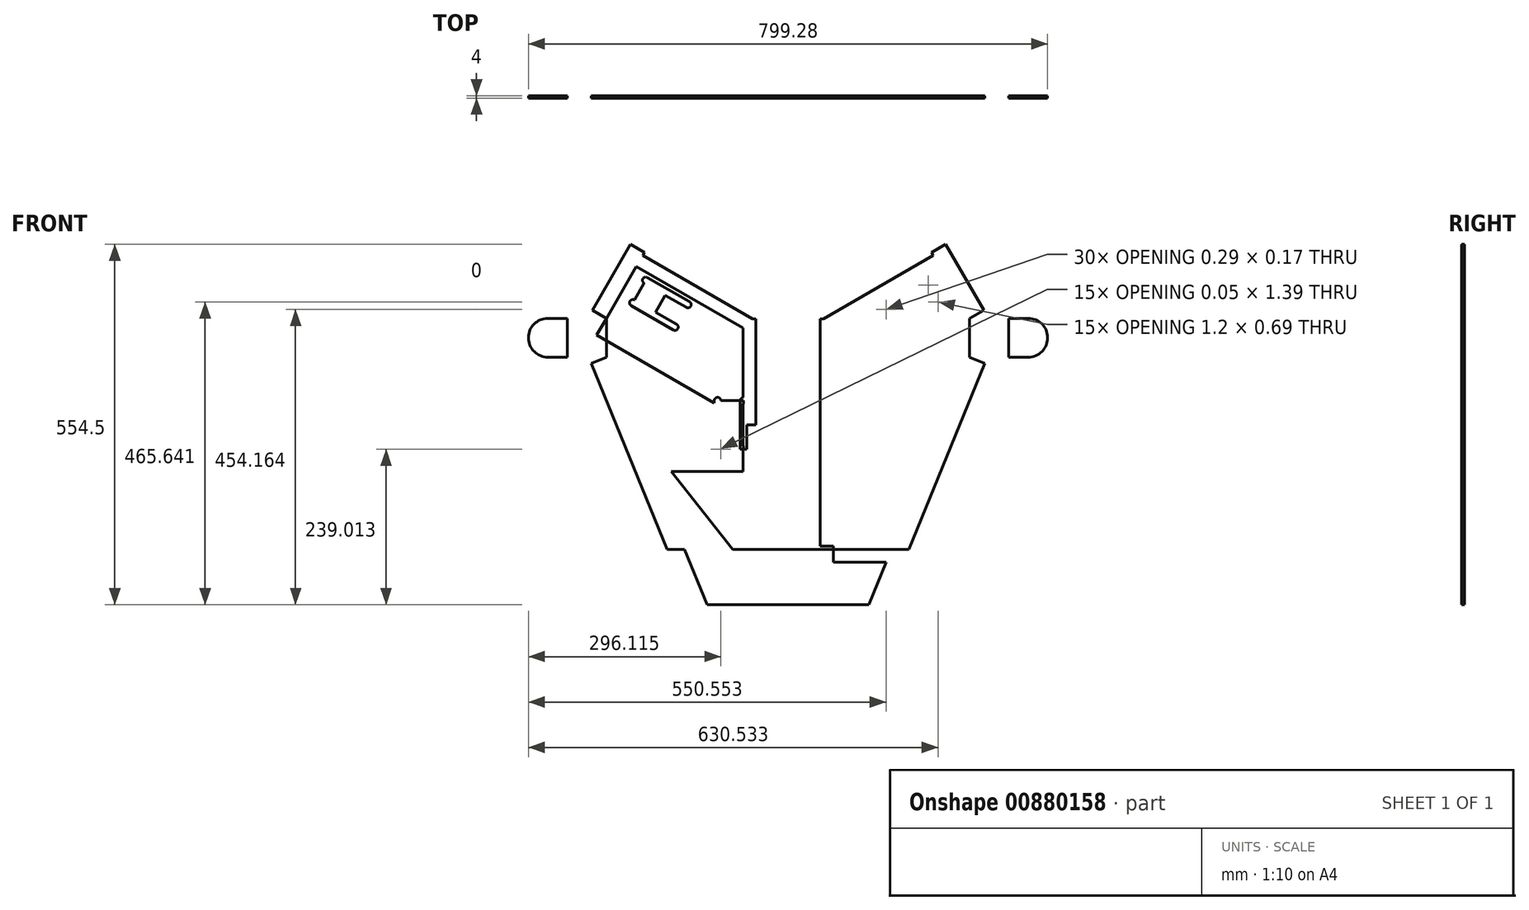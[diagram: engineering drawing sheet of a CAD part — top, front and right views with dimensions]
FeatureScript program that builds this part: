
annotation { "Feature Type Name" : "Feature", "Feature Type Description" : "" }
export const myFeature = defineFeature(function(context is Context, id is Id, definition is map)
    precondition{}
    {
        {
            var Q0;
            Q0=qCreatedBy(makeId("Front.planeOp"),FACE);
            var sketch = newSketch(context, id + "F0", { "sketchPlane" : qUnion([Q0])});
            skLineSegment(sketch, "E0", {"start": v(-53.14, 78.62) * mm, "end": v(-53.14, -271.38) * mm});
            skLineSegment(sketch, "E1", {"start": v(-53.14, -271.38) * mm, "end": v(-28.14, -271.38) * mm});
            skLineSegment(sketch, "E2", {"start": v(-28.14, -271.38) * mm, "end": v(-28.14, 78.62) * mm});
            skLineSegment(sketch, "E3", {"start": v(-28.14, 78.62) * mm, "end": v(-53.14, 78.62) * mm});
            skLineSegment(sketch, "E4", {"start": v(-28.14, 78.62) * mm, "end": v(-331.25, 253.62) * mm});
            skLineSegment(sketch, "E5", {"start": v(-331.25, 253.62) * mm, "end": v(-343.75, 231.97) * mm});
            skLineSegment(sketch, "E6", {"start": v(-343.75, 231.97) * mm, "end": v(-53.14, 64.19) * mm});
            skLineSegment(sketch, "E7", {"start": v(-53.14, -271.38) * mm, "end": v(-53.14, -296.38) * mm});
            skLineSegment(sketch, "E8", {"start": v(-53.14, -296.38) * mm, "end": v(85.86, -296.38) * mm});
            skLineSegment(sketch, "E9", {"start": v(85.86, -296.38) * mm, "end": v(85.86, -271.38) * mm});
            skLineSegment(sketch, "E10", {"start": v(85.86, -271.38) * mm, "end": v(-28.14, -271.38) * mm});
            skLineSegment(sketch, "E11", {"start": v(85.86, -271.38) * mm, "end": v(85.86, 78.62) * mm});
            skLineSegment(sketch, "E12", {"start": v(85.86, 78.62) * mm, "end": v(60.86, 78.62) * mm});
            skLineSegment(sketch, "E13", {"start": v(60.86, 78.62) * mm, "end": v(60.86, -271.38) * mm});
            skLineSegment(sketch, "E14", {"start": v(60.86, 78.62) * mm, "end": v(363.97, 253.62) * mm});
            skLineSegment(sketch, "E15", {"start": v(363.97, 253.62) * mm, "end": v(376.47, 231.97) * mm});
            skLineSegment(sketch, "E16", {"start": v(376.47, 231.97) * mm, "end": v(85.86, 64.19) * mm});
            skLineSegment(sketch, "E17", {"start": v(-331.25, 253.62) * mm, "end": v(-333.75, 249.3) * mm});
            skLineSegment(sketch, "E18", {"start": v(-333.75, 249.3) * mm, "end": v(-38.14, 78.62) * mm});
            skLineSegment(sketch, "E19", {"start": v(-28.14, 78.62) * mm, "end": v(-33.14, 78.62) * mm});
            skLineSegment(sketch, "E20", {"start": v(-33.14, 78.62) * mm, "end": v(-33.14, -271.38) * mm});
            skLineSegment(sketch, "E21", {"start": v(-53.14, -271.38) * mm, "end": v(-53.14, -276.38) * mm});
            skLineSegment(sketch, "E22", {"start": v(-53.14, -276.38) * mm, "end": v(85.86, -276.38) * mm});
            skLineSegment(sketch, "E23", {"start": v(60.86, -271.38) * mm, "end": v(65.86, -271.38) * mm});
            skLineSegment(sketch, "E24", {"start": v(65.86, -271.38) * mm, "end": v(65.86, 78.62) * mm});
            skPoint(sketch, "E24.endSnap0", {"position": v(73.36, 78.62) * mm});
            skLineSegment(sketch, "E25", {"start": v(363.97, 253.62) * mm, "end": v(366.47, 249.3) * mm});
            skLineSegment(sketch, "E26", {"start": v(366.47, 249.3) * mm, "end": v(70.86, 78.62) * mm});
            skLineSegment(sketch, "E27", {"start": v(-176.95, 121.87) * mm, "end": v(-228.9, 151.87) * mm});
            skLineSegment(sketch, "E28", {"start": v(-305.46, 69.05) * mm, "end": v(-53.14, -76.62) * mm});
            skLineSegment(sketch, "E29", {"start": v(-53.14, -51.52) * mm, "end": v(-53.14, -71.28) * mm});
            skLineSegment(sketch, "E30", {"start": v(-53.14, -71.28) * mm, "end": v(-53.14, -131.28) * mm});
            skLineSegment(sketch, "E31", {"start": v(-53.14, -156.38) * mm, "end": v(-163.14, -156.38) * mm});
            skLineSegment(sketch, "E32", {"start": v(-163.14, -156.38) * mm, "end": v(-163.14, -13.11) * mm});
            skLineSegment(sketch, "E33", {"start": v(-163.14, -156.38) * mm, "end": v(-53.14, -296.38) * mm});
            skLineSegment(sketch, "E34", {"start": v(85.86, -156.38) * mm, "end": v(195.86, -156.38) * mm});
            skLineSegment(sketch, "E35", {"start": v(195.86, -156.38) * mm, "end": v(85.86, -296.38) * mm});
            skLineSegment(sketch, "E36", {"start": v(195.86, -156.38) * mm, "end": v(195.86, -13.11) * mm});
            skLineSegment(sketch, "E37", {"start": v(85.86, -76.62) * mm, "end": v(195.86, -13.11) * mm});
            skLineSegment(sketch, "E38", {"start": v(195.86, -13.11) * mm, "end": v(338.18, 69.05) * mm});
            skLineSegment(sketch, "E39", {"start": v(-250.4, 178.08) * mm, "end": v(-237.9, 199.73) * mm});
            skLineSegment(sketch, "E40", {"start": v(277.2, 174.66) * mm, "end": v(264.7, 196.31) * mm});
            skLineSegment(sketch, "E41", {"start": v(264.7, 196.31) * mm, "end": v(338.18, 196.31) * mm});
            skLineSegment(sketch, "E42", {"start": v(-108.14, -226.38) * mm, "end": v(-108.14, -296.38) * mm});
            skLineSegment(sketch, "E43", {"start": v(-108.14, -296.38) * mm, "end": v(-53.14, -296.38) * mm});
            skLineSegment(sketch, "E44", {"start": v(85.86, -296.38) * mm, "end": v(140.86, -296.38) * mm});
            skPoint(sketch, "E44.endSnap0", {"position": v(140.86, -226.38) * mm});
            skLineSegment(sketch, "E45", {"start": v(140.86, -296.38) * mm, "end": v(140.86, -226.38) * mm});
            skLineSegment(sketch, "E46", {"start": v(-158.2, 139.92) * mm, "end": v(-208.2, 53.31) * mm});
            skLineSegment(sketch, "E47", {"start": v(-158.2, 139.92) * mm, "end": v(-168.95, 121.3) * mm});
            skLineSegment(sketch, "E48", {"start": v(-168.95, 121.3) * mm, "end": v(-201.42, 140.05) * mm});
            skLineSegment(sketch, "E49", {"start": v(-201.42, 140.05) * mm, "end": v(-202.67, 137.88) * mm});
            skLineSegment(sketch, "E50", {"start": v(-202.67, 137.88) * mm, "end": v(-137.72, 100.38) * mm});
            skCircle(sketch, "E51", {"center": v(-202.67, 137.88) * mm, "radius": 5 * mm});
            skCircle(sketch, "E52", {"center": v(-137.72, 100.38) * mm, "radius": 5 * mm});
            skLineSegment(sketch, "E53", {"start": v(-135.37, 104.8) * mm, "end": v(-140.07, 95.97) * mm});
            skLineSegment(sketch, "E54", {"start": v(-140.07, 95.97) * mm, "end": v(-205.31, 133.64) * mm});
            skLineSegment(sketch, "E55", {"start": v(-202.67, 137.88) * mm, "end": v(-222.67, 103.24) * mm});
            skLineSegment(sketch, "E56", {"start": v(-222.67, 103.24) * mm, "end": v(-157.72, 65.74) * mm});
            skCircle(sketch, "E57", {"center": v(-222.67, 103.24) * mm, "radius": 5 * mm});
            skCircle(sketch, "E58", {"center": v(-157.72, 65.74) * mm, "radius": 5 * mm});
            skLineSegment(sketch, "E59", {"start": v(-155.22, 70.07) * mm, "end": v(-220.17, 107.57) * mm});
            skLineSegment(sketch, "E60", {"start": v(-220.17, 107.57) * mm, "end": v(-225.17, 98.9) * mm});
            skLineSegment(sketch, "E61", {"start": v(-225.17, 98.9) * mm, "end": v(-160.22, 61.4) * mm});
            skLineSegment(sketch, "E62", {"start": v(-200.1, 142.17) * mm, "end": v(-135.37, 104.8) * mm});
            skLineSegment(sketch, "E63", {"start": v(-28.14, -84.86) * mm, "end": v(-49.64, -84.86) * mm});
            skLineSegment(sketch, "E64", {"start": v(-49.64, -84.86) * mm, "end": v(-49.64, -47.36) * mm});
            skLineSegment(sketch, "E65", {"start": v(-49.64, -47.36) * mm, "end": v(-52.14, -47.36) * mm});
            skLineSegment(sketch, "E66", {"start": v(-52.14, -47.36) * mm, "end": v(-52.14, -122.36) * mm});
            skCircle(sketch, "E67", {"center": v(-52.14, -47.36) * mm, "radius": 5 * mm});
            skCircle(sketch, "E68", {"center": v(-52.14, -122.36) * mm, "radius": 5 * mm});
            skLineSegment(sketch, "E69", {"start": v(-47.14, -122.2) * mm, "end": v(-57.14, -122.53) * mm});
            skLineSegment(sketch, "E70", {"start": v(-57.14, -122.53) * mm, "end": v(-57.14, -47.2) * mm});
            skLineSegment(sketch, "E71", {"start": v(-52.14, -47.36) * mm, "end": v(-92.14, -47.36) * mm});
            skLineSegment(sketch, "E72", {"start": v(-92.14, -47.36) * mm, "end": v(-92.14, -122.36) * mm});
            skCircle(sketch, "E73", {"center": v(-92.14, -47.36) * mm, "radius": 5 * mm});
            skCircle(sketch, "E74", {"center": v(-92.14, -122.36) * mm, "radius": 5 * mm});
            skLineSegment(sketch, "E75", {"start": v(-87.19, -123.06) * mm, "end": v(-87.14, -47.36) * mm});
            skLineSegment(sketch, "E76", {"start": v(-87.14, -47.36) * mm, "end": v(-97.14, -47.36) * mm});
            skLineSegment(sketch, "E77", {"start": v(-97.14, -47.36) * mm, "end": v(-97.14, -122.36) * mm});
            skLineSegment(sketch, "E78", {"start": v(-47.14, -47.44) * mm, "end": v(-47.14, -122.2) * mm});
            skLineSegment(sketch, "E79", {"start": v(185.25, 136.65) * mm, "end": v(196, 118.03) * mm});
            skLineSegment(sketch, "E80", {"start": v(196, 118.03) * mm, "end": v(163.52, 99.28) * mm});
            skLineSegment(sketch, "E81", {"start": v(163.52, 99.28) * mm, "end": v(164.77, 97.11) * mm});
            skLineSegment(sketch, "E82", {"start": v(164.77, 97.11) * mm, "end": v(229.73, 134.61) * mm});
            skCircle(sketch, "E83", {"center": v(164.77, 97.11) * mm, "radius": 5 * mm});
            skCircle(sketch, "E84", {"center": v(229.73, 134.61) * mm, "radius": 5 * mm});
            skLineSegment(sketch, "E85", {"start": v(227.08, 138.86) * mm, "end": v(232.37, 130.37) * mm});
            skLineSegment(sketch, "E86", {"start": v(232.37, 130.37) * mm, "end": v(167.13, 92.7) * mm});
            skLineSegment(sketch, "E87", {"start": v(164.77, 97.11) * mm, "end": v(184.77, 62.47) * mm});
            skLineSegment(sketch, "E88", {"start": v(184.77, 62.47) * mm, "end": v(249.73, 99.97) * mm});
            skCircle(sketch, "E89", {"center": v(184.77, 62.47) * mm, "radius": 5 * mm});
            skCircle(sketch, "E90", {"center": v(249.73, 99.97) * mm, "radius": 5 * mm});
            skLineSegment(sketch, "E91", {"start": v(247.86, 104.6) * mm, "end": v(182.27, 66.8) * mm});
            skLineSegment(sketch, "E92", {"start": v(182.27, 66.8) * mm, "end": v(187.27, 58.14) * mm});
            skLineSegment(sketch, "E93", {"start": v(187.27, 58.14) * mm, "end": v(252.23, 95.64) * mm});
            skLineSegment(sketch, "E94", {"start": v(162.34, 101.48) * mm, "end": v(227.08, 138.86) * mm});
            skLineSegment(sketch, "E95", {"start": v(185.25, 136.65) * mm, "end": v(158.33, 121.1) * mm});
            skLineSegment(sketch, "E96", {"start": v(-158.2, 139.92) * mm, "end": v(-136.54, 127.42) * mm});
            skLineSegment(sketch, "E97", {"start": v(-28.14, -84.86) * mm, "end": v(-28.14, -59.86) * mm});
            skLineSegment(sketch, "E98", {"start": v(-208.2, 53.31) * mm, "end": v(-208.2, -33.23) * mm});
            skLineSegment(sketch, "E99", {"start": v(-208.2, -33.23) * mm, "end": v(-163.14, -33.23) * mm});
            skLineSegment(sketch, "E100", {"start": v(195.86, -33.23) * mm, "end": v(240.91, -33.23) * mm});
            skLineSegment(sketch, "E101", {"start": v(240.91, -33.23) * mm, "end": v(240.91, 12.9) * mm});
            skLineSegment(sketch, "E102", {"start": v(-208.2, 12.9) * mm, "end": v(-208.2, 32.9) * mm});
            skLineSegment(sketch, "E103", {"start": v(240.91, 12.9) * mm, "end": v(240.91, 32.9) * mm});
            skLineSegment(sketch, "E104", {"start": v(-163.14, -84.74) * mm, "end": v(-180.4, -84.74) * mm});
            skLineSegment(sketch, "E105", {"start": v(-180.4, -84.74) * mm, "end": v(-180.4, -33.23) * mm});
            skLineSegment(sketch, "E106", {"start": v(-28.14, 78.62) * mm, "end": v(-204.8, 180.62) * mm});
            skLineSegment(sketch, "E107", {"start": v(-204.8, 180.62) * mm, "end": v(-278.28, 53.37) * mm});
            skLineSegment(sketch, "E108", {"start": v(60.86, 78.62) * mm, "end": v(237.53, 180.62) * mm});
            skLineSegment(sketch, "E109", {"start": v(237.53, 180.62) * mm, "end": v(311, 53.37) * mm});
            skLineSegment(sketch, "E110", {"start": v(-108.14, -296.38) * mm, "end": v(-108.14, -361.38) * mm});
            skLineSegment(sketch, "E111", {"start": v(-108.14, -361.38) * mm, "end": v(140.86, -361.38) * mm});
            skLineSegment(sketch, "E112", {"start": v(140.86, -361.38) * mm, "end": v(140.86, -296.38) * mm});
            skLineSegment(sketch, "E113", {"start": v(-278.28, 53.37) * mm, "end": v(-263.28, 79.35) * mm});
            skLineSegment(sketch, "E114", {"start": v(-263.28, 79.35) * mm, "end": v(-323.28, 79.35) * mm});
            skLineSegment(sketch, "E115", {"start": v(-323.28, 79.35) * mm, "end": v(-323.28, 19.35) * mm});
            skLineSegment(sketch, "E116", {"start": v(-323.28, 19.35) * mm, "end": v(-219.36, 19.35) * mm});
            skLineSegment(sketch, "E117", {"start": v(311, 53.37) * mm, "end": v(296, 79.35) * mm});
            skLineSegment(sketch, "E118", {"start": v(296, 79.35) * mm, "end": v(356, 79.35) * mm});
            skLineSegment(sketch, "E119", {"start": v(356, 79.35) * mm, "end": v(356, 19.35) * mm});
            skLineSegment(sketch, "E120", {"start": v(356, 19.35) * mm, "end": v(252.08, 19.35) * mm});
            skLineSegment(sketch, "E121", {"start": v(-263.28, 79.35) * mm, "end": v(-263.28, 19.35) * mm});
            skLineSegment(sketch, "E122", {"start": v(-263.28, 19.35) * mm, "end": v(-108.14, -361.38) * mm});
            skLineSegment(sketch, "E123", {"start": v(296, 79.35) * mm, "end": v(296, 19.35) * mm});
            skLineSegment(sketch, "E124", {"start": v(296, 19.35) * mm, "end": v(140.86, -361.38) * mm});
            skLineSegment(sketch, "E125", {"start": v(-28.14, -271.38) * mm, "end": v(-28.14, -251.38) * mm});
            skLineSegment(sketch, "E126", {"start": v(-28.14, -251.38) * mm, "end": v(60.86, -251.38) * mm});
            skLineSegment(sketch, "E127", {"start": v(-108.14, -361.38) * mm, "end": v(-108.14, -386.38) * mm});
            skLineSegment(sketch, "E128", {"start": v(-108.14, -386.38) * mm, "end": v(140.86, -386.38) * mm});
            skLineSegment(sketch, "E129", {"start": v(140.86, -386.38) * mm, "end": v(140.86, -361.38) * mm});
            skLineSegment(sketch, "E130", {"start": v(140.86, -361.38) * mm, "end": v(164.01, -370.81) * mm});
            skLineSegment(sketch, "E131", {"start": v(164.01, -370.81) * mm, "end": v(319.15, 9.91) * mm});
            skLineSegment(sketch, "E132", {"start": v(319.15, 9.91) * mm, "end": v(296, 19.35) * mm});
            skLineSegment(sketch, "E133", {"start": v(-108.14, -361.38) * mm, "end": v(-131.3, -370.81) * mm});
            skLineSegment(sketch, "E134", {"start": v(-131.3, -370.81) * mm, "end": v(-286.43, 9.91) * mm});
            skLineSegment(sketch, "E135", {"start": v(-286.43, 9.91) * mm, "end": v(-263.28, 19.35) * mm});
            skLineSegment(sketch, "E136", {"start": v(-323.28, 19.35) * mm, "end": v(-383.28, 19.35) * mm});
            skLineSegment(sketch, "E137", {"start": v(-383.28, 19.35) * mm, "end": v(-383.28, 79.35) * mm});
            skLineSegment(sketch, "E138", {"start": v(-383.28, 79.35) * mm, "end": v(-323.28, 79.35) * mm});
            skCircle(sketch, "E139", {"center": v(-353.28, 49.35) * mm, "radius": 30 * mm});
            skPoint(sketch, "E139.centerSnap0", {"position": v(-383.28, 49.35) * mm});
            skPoint(sketch, "E139.centerSnap1", {"position": v(-353.28, 79.35) * mm});
            skLineSegment(sketch, "E140", {"start": v(-263.28, 79.35) * mm, "end": v(-284.93, 91.85) * mm});
            skLineSegment(sketch, "E141", {"start": v(-284.93, 91.85) * mm, "end": v(-238.96, 171.47) * mm});
            skLineSegment(sketch, "E142", {"start": v(-238.96, 171.47) * mm, "end": v(-226.46, 193.12) * mm});
            skLineSegment(sketch, "E143", {"start": v(-204.8, 180.62) * mm, "end": v(-192.3, 202.27) * mm});
            skLineSegment(sketch, "E144", {"start": v(-28.14, 78.62) * mm, "end": v(-15.64, 100.27) * mm});
            skLineSegment(sketch, "E145", {"start": v(-15.64, 100.27) * mm, "end": v(-192.3, 202.27) * mm});
            skLineSegment(sketch, "E146", {"start": v(60.86, 78.62) * mm, "end": v(48.36, 100.27) * mm});
            skLineSegment(sketch, "E147", {"start": v(237.53, 180.62) * mm, "end": v(225.03, 202.27) * mm});
            skLineSegment(sketch, "E148", {"start": v(225.03, 202.27) * mm, "end": v(48.36, 100.27) * mm});
            skLineSegment(sketch, "E149", {"start": v(296, 79.35) * mm, "end": v(317.65, 91.85) * mm});
            skLineSegment(sketch, "E150", {"start": v(317.65, 91.85) * mm, "end": v(259.18, 193.12) * mm});
            skLineSegment(sketch, "E151", {"start": v(356, 19.35) * mm, "end": v(416, 19.35) * mm});
            skLineSegment(sketch, "E152", {"start": v(416, 19.35) * mm, "end": v(416, 79.35) * mm});
            skLineSegment(sketch, "E153", {"start": v(416, 79.35) * mm, "end": v(356, 79.35) * mm});
            skCircle(sketch, "E154", {"center": v(386, 49.35) * mm, "radius": 30 * mm});
            skPoint(sketch, "E154.centerSnap0", {"position": v(416, 49.35) * mm});
            skPoint(sketch, "E154.centerSnap1", {"position": v(386, 19.35) * mm});
            skLineSegment(sketch, "E155", {"start": v(-108.14, -361.38) * mm, "end": v(-135.14, -361.38) * mm});
            skLineSegment(sketch, "E156", {"start": v(-135.14, -361.38) * mm, "end": v(140.86, -361.38) * mm});
            skLineSegment(sketch, "E157", {"start": v(140.86, -361.38) * mm, "end": v(167.86, -361.38) * mm});
            skLineSegment(sketch, "E158", {"start": v(-108.14, -296.38) * mm, "end": v(-161.62, -296.38) * mm});
            skLineSegment(sketch, "E159", {"start": v(-161.62, -296.38) * mm, "end": v(194.34, -296.38) * mm});
            skLineSegment(sketch, "E160", {"start": v(85.86, -276.38) * mm, "end": v(202.5, -276.38) * mm});
            skLineSegment(sketch, "E161", {"start": v(202.5, -276.38) * mm, "end": v(-169.77, -276.38) * mm});
            skSolve(sketch);
        }
        {
            var Q0;
            Q0=makeQuery(id+"F0.imprint","IMPRINT",FACE,{"disambiguationData":[TD([[makeQuery(id+"F0.imprint","IMPRINT",EDGE,{"derivedFrom":sQuery(id+"F0.wireOp",EDGE,"E106")}),-1.0]])]});
            var Q1;
            Q1=makeQuery(id+"F0.imprint","IMPRINT",FACE,{"disambiguationData":[TD([[makeQuery(id+"F0.imprint","IMPRINT",EDGE,{"derivedFrom":sQuery(id+"F0.wireOp",EDGE,"E108")}),1.0]])]});
            var Q2;
            {var subQ5=sQuery(id+"F0.wireOp",EDGE,"E149");Q2=makeQuery(id+"F0.imprint","IMPRINT",FACE,{"disambiguationData":[TD([[makeQuery(id+"F0.imprint","IMPRINT",EDGE,{"derivedFrom":subQ5}),1.0]])]});}
            var Q3;
            {var subQ0=sQuery(id+"F0.wireOp",EDGE,"E113");Q3=makeQuery(id+"F0.imprint","IMPRINT",FACE,{"disambiguationData":[TD([[makeQuery(id+"F0.imprint","IMPRINT",EDGE,{"derivedFrom":subQ0}),-1.0]])]});}
            var Q4;
            {var subQ0=sQuery(id+"F0.wireOp",EDGE,"E117");Q4=makeQuery(id+"F0.imprint","IMPRINT",FACE,{"disambiguationData":[TD([[makeQuery(id+"F0.imprint","IMPRINT",EDGE,{"derivedFrom":subQ0}),1.0]])]});}
            var Q5;
            {var subQ0=sQuery(id+"F0.wireOp",EDGE,"E138");var subQ3=sQuery(id+"F0.wireOp",EDGE,"E139");var subQ5=makeQuery(id+"F0.imprint","INTERSECT",VERTEX,{"derivedFrom":[subQ0,subQ3]});Q5=makeQuery(id+"F0.imprint","IMPRINT",FACE,{"disambiguationData":[TD([[makeQuery(id+"F0.imprint","IMPRINT",EDGE,{"disambiguationData":[TD([[subQ5,1.0]])],"derivedFrom":subQ3}),-1.0]])]});}
            var Q6;
            {var subQ0=sQuery(id+"F0.wireOp",EDGE,"E136");var subQ3=sQuery(id+"F0.wireOp",EDGE,"E139");var subQ5=makeQuery(id+"F0.imprint","INTERSECT",VERTEX,{"derivedFrom":[subQ0,subQ3]});Q6=makeQuery(id+"F0.imprint","IMPRINT",FACE,{"disambiguationData":[TD([[makeQuery(id+"F0.imprint","IMPRINT",EDGE,{"disambiguationData":[TD([[subQ5,-1.0]])],"derivedFrom":subQ3}),-1.0]])]});}
            var Q7;
            {var subQ0=sQuery(id+"F0.wireOp",EDGE,"E153");var subQ3=sQuery(id+"F0.wireOp",EDGE,"E154");var subQ5=makeQuery(id+"F0.imprint","INTERSECT",VERTEX,{"derivedFrom":[subQ0,subQ3]});Q7=makeQuery(id+"F0.imprint","IMPRINT",FACE,{"disambiguationData":[TD([[makeQuery(id+"F0.imprint","IMPRINT",EDGE,{"disambiguationData":[TD([[subQ5,-1.0]])],"derivedFrom":subQ3}),-1.0]])]});}
            var Q8;
            {var subQ0=sQuery(id+"F0.wireOp",EDGE,"E151");var subQ3=sQuery(id+"F0.wireOp",EDGE,"E154");var subQ5=makeQuery(id+"F0.imprint","INTERSECT",VERTEX,{"derivedFrom":[subQ0,subQ3]});Q8=makeQuery(id+"F0.imprint","IMPRINT",FACE,{"disambiguationData":[TD([[makeQuery(id+"F0.imprint","IMPRINT",EDGE,{"disambiguationData":[TD([[subQ5,1.0]])],"derivedFrom":subQ3}),-1.0]])]});}
            var Q9;
            {var subQ1=sQuery(id+"F0.wireOp",EDGE,"E19");Q9=makeQuery(id+"F0.imprint","IMPRINT",FACE,{"disambiguationData":[TD([[makeQuery(id+"F0.imprint","IMPRINT",EDGE,{"derivedFrom":subQ1}),1.0]])]});}
            var Q10;
            {var subQ3=sQuery(id+"F0.wireOp",EDGE,"E142");var subQ5=sQuery(id+"F0.wireOp",EDGE,"E18");var subQ7=makeQuery(id+"F0.imprint","INTERSECT",VERTEX,{"derivedFrom":[subQ5,subQ3]});Q10=makeQuery(id+"F0.imprint","IMPRINT",FACE,{"disambiguationData":[TD([[makeQuery(id+"F0.imprint","IMPRINT",EDGE,{"disambiguationData":[TD([[subQ7,-1.0]])],"derivedFrom":subQ5}),1.0]])]});}
            var Q11;
            {var subQ0=sQuery(id+"F0.wireOp",EDGE,"E140");Q11=makeQuery(id+"F0.imprint","IMPRINT",FACE,{"disambiguationData":[TD([[makeQuery(id+"F0.imprint","IMPRINT",EDGE,{"derivedFrom":subQ0}),-1.0]])]});}
            var Q12;
            {var subQ0=sQuery(id+"F0.wireOp",EDGE,"E125");Q12=makeQuery(id+"F0.imprint","IMPRINT",FACE,{"disambiguationData":[TD([[makeQuery(id+"F0.imprint","IMPRINT",EDGE,{"derivedFrom":subQ0}),-1.0]])]});}
            var Q13;
            {var subQ3=sQuery(id+"F0.wireOp",EDGE,"E150");var subQ5=sQuery(id+"F0.wireOp",EDGE,"E26");var subQ6=makeQuery(id+"F0.imprint","INTERSECT",VERTEX,{"derivedFrom":[subQ5,subQ3]});Q13=makeQuery(id+"F0.imprint","IMPRINT",FACE,{"disambiguationData":[TD([[makeQuery(id+"F0.imprint","IMPRINT",EDGE,{"disambiguationData":[TD([[subQ6,-1.0]])],"derivedFrom":subQ5}),-1.0]])]});}
            var Q14;
            {var subQ0=sQuery(id+"F0.wireOp",EDGE,"E116");var subQ1=sQuery(id+"F0.wireOp",EDGE,"E28");var subQ2=makeQuery(id+"F0.imprint","INTERSECT",VERTEX,{"derivedFrom":[subQ1,subQ0]});Q14=makeQuery(id+"F0.imprint","IMPRINT",FACE,{"disambiguationData":[TD([[makeQuery(id+"F0.imprint","IMPRINT",EDGE,{"disambiguationData":[TD([[subQ2,1.0]])],"derivedFrom":subQ1}),-1.0]])]});}
            var Q15;
            {var subQ0=sQuery(id+"F0.wireOp",EDGE,"E120");var subQ1=sQuery(id+"F0.wireOp",EDGE,"E38");var subQ2=makeQuery(id+"F0.imprint","INTERSECT",VERTEX,{"derivedFrom":[subQ1,subQ0]});Q15=makeQuery(id+"F0.imprint","IMPRINT",FACE,{"disambiguationData":[TD([[makeQuery(id+"F0.imprint","IMPRINT",EDGE,{"disambiguationData":[TD([[subQ2,-1.0]])],"derivedFrom":subQ1}),-1.0]])]});}
            var Q16;
            {var subQ5=sQuery(id+"F0.wireOp",EDGE,"E125");Q16=makeQuery(id+"F0.imprint","IMPRINT",FACE,{"disambiguationData":[TD([[makeQuery(id+"F0.imprint","IMPRINT",EDGE,{"derivedFrom":subQ5}),1.0]])]});}
            var Q17;
            {var subQ0=sQuery(id+"F0.wireOp",EDGE,"E142");var subQ5=sQuery(id+"F0.wireOp",EDGE,"E18");var subQ6=makeQuery(id+"F0.imprint","INTERSECT",VERTEX,{"derivedFrom":[subQ5,subQ0]});Q17=makeQuery(id+"F0.imprint","IMPRINT",FACE,{"disambiguationData":[TD([[makeQuery(id+"F0.imprint","IMPRINT",EDGE,{"disambiguationData":[TD([[subQ6,-1.0]])],"derivedFrom":subQ5}),-1.0]])]});}
            var Q18;
            {var subQ0=sQuery(id+"F0.wireOp",EDGE,"E23");Q18=makeQuery(id+"F0.imprint","IMPRINT",FACE,{"disambiguationData":[TD([[makeQuery(id+"F0.imprint","IMPRINT",EDGE,{"derivedFrom":subQ0}),1.0]])]});}
            var Q19;
            {var subQ0=sQuery(id+"F0.wireOp",EDGE,"E150");var subQ1=sQuery(id+"F0.wireOp",EDGE,"E16");var subQ2=makeQuery(id+"F0.imprint","INTERSECT",VERTEX,{"derivedFrom":[subQ1,subQ0]});Q19=makeQuery(id+"F0.imprint","IMPRINT",FACE,{"disambiguationData":[TD([[makeQuery(id+"F0.imprint","IMPRINT",EDGE,{"disambiguationData":[TD([[subQ2,-1.0]])],"derivedFrom":subQ1}),-1.0]])]});}
            var Q20;
            {var subQ8=sQuery(id+"F0.wireOp",EDGE,"E113");Q20=makeQuery(id+"F0.imprint","IMPRINT",FACE,{"disambiguationData":[TD([[makeQuery(id+"F0.imprint","IMPRINT",EDGE,{"derivedFrom":subQ8}),1.0]])]});}
            var Q21;
            {var subQ8=sQuery(id+"F0.wireOp",EDGE,"E117");Q21=makeQuery(id+"F0.imprint","IMPRINT",FACE,{"disambiguationData":[TD([[makeQuery(id+"F0.imprint","IMPRINT",EDGE,{"derivedFrom":subQ8}),-1.0]])]});}
            var Q22;
            {var subQ0=sQuery(id+"F0.wireOp",EDGE,"E139");var subQ1=makeQuery(id+"F0.imprint","INTERSECT",VERTEX,{"derivedFrom":[sQuery(id+"F0.wireOp",EDGE,"E138"),subQ0]});Q22=makeQuery(id+"F0.imprint","IMPRINT",FACE,{"disambiguationData":[TD([[makeQuery(id+"F0.imprint","IMPRINT",EDGE,{"disambiguationData":[TD([[subQ1,1.0]])],"derivedFrom":subQ0}),1.0]])]});}
            var Q23;
            {var subQ0=sQuery(id+"F0.wireOp",EDGE,"E154");var subQ1=makeQuery(id+"F0.imprint","INTERSECT",VERTEX,{"derivedFrom":[sQuery(id+"F0.wireOp",EDGE,"E152"),subQ0]});Q23=makeQuery(id+"F0.imprint","IMPRINT",FACE,{"disambiguationData":[TD([[makeQuery(id+"F0.imprint","IMPRINT",EDGE,{"disambiguationData":[TD([[subQ1,-1.0]])],"derivedFrom":subQ0}),1.0]])]});}
            var Q24;
            {var subQ6=sQuery(id+"F0.wireOp",EDGE,"E19");Q24=makeQuery(id+"F0.imprint","IMPRINT",FACE,{"disambiguationData":[TD([[makeQuery(id+"F0.imprint","IMPRINT",EDGE,{"derivedFrom":subQ6}),-1.0]])]});}
            var Q25;
            {var subQ0=sQuery(id+"F0.wireOp",EDGE,"E108");Q25=makeQuery(id+"F0.imprint","IMPRINT",FACE,{"disambiguationData":[TD([[makeQuery(id+"F0.imprint","IMPRINT",EDGE,{"derivedFrom":subQ0}),-1.0]])]});}
            var Q26;
            {var subQ3=sQuery(id+"F0.wireOp",EDGE,"E161");var subQ5=sQuery(id+"F0.wireOp",EDGE,"E124");var subQ6=makeQuery(id+"F0.imprint","INTERSECT",VERTEX,{"derivedFrom":[subQ5,subQ3]});Q26=makeQuery(id+"F0.imprint","IMPRINT",FACE,{"disambiguationData":[TD([[makeQuery(id+"F0.imprint","IMPRINT",EDGE,{"disambiguationData":[TD([[subQ6,-1.0]])],"derivedFrom":subQ5}),-1.0]])]});}
            var Q27;
            {var subQ3=sQuery(id+"F0.wireOp",EDGE,"E161");var subQ5=sQuery(id+"F0.wireOp",EDGE,"E122");var subQ6=makeQuery(id+"F0.imprint","INTERSECT",VERTEX,{"derivedFrom":[subQ5,subQ3]});Q27=makeQuery(id+"F0.imprint","IMPRINT",FACE,{"disambiguationData":[TD([[makeQuery(id+"F0.imprint","IMPRINT",EDGE,{"disambiguationData":[TD([[subQ6,-1.0]])],"derivedFrom":subQ5}),1.0]])]});}
            var Q28;
            {var subQ19=sQuery(id+"F0.wireOp",EDGE,"E102");Q28=makeQuery(id+"F0.imprint","IMPRINT",FACE,{"disambiguationData":[TD([[makeQuery(id+"F0.imprint","IMPRINT",EDGE,{"derivedFrom":subQ19}),1.0]])]});}
            var Q29;
            {var subQ19=sQuery(id+"F0.wireOp",EDGE,"E37");Q29=makeQuery(id+"F0.imprint","IMPRINT",FACE,{"disambiguationData":[TD([[makeQuery(id+"F0.imprint","IMPRINT",EDGE,{"derivedFrom":subQ19}),1.0]])]});}
            var Q30;
            {var subQ24=sQuery(id+"F0.wireOp",EDGE,"E102");Q30=makeQuery(id+"F0.imprint","IMPRINT",FACE,{"disambiguationData":[TD([[makeQuery(id+"F0.imprint","IMPRINT",EDGE,{"derivedFrom":subQ24}),-1.0]])]});}
            var Q31;
            {var subQ4=sQuery(id+"F0.wireOp",EDGE,"E3");var subQ5=sQuery(id+"F0.wireOp",EDGE,"E0");var subQ6=makeQuery(id+"F0.imprint","INTERSECT",VERTEX,{"derivedFrom":[subQ5,subQ4]});Q31=makeQuery(id+"F0.imprint","IMPRINT",FACE,{"disambiguationData":[TD([[makeQuery(id+"F0.imprint","IMPRINT",EDGE,{"disambiguationData":[TD([[subQ6,-1.0]])],"derivedFrom":subQ5}),-1.0]])]});}
            var Q32;
            {var subQ12=sQuery(id+"F0.wireOp",EDGE,"E31");Q32=makeQuery(id+"F0.imprint","IMPRINT",FACE,{"disambiguationData":[TD([[makeQuery(id+"F0.imprint","IMPRINT",EDGE,{"derivedFrom":subQ12}),-1.0]])]});}
            var Q33;
            {var subQ3=sQuery(id+"F0.wireOp",EDGE,"E104");Q33=makeQuery(id+"F0.imprint","IMPRINT",FACE,{"disambiguationData":[TD([[makeQuery(id+"F0.imprint","IMPRINT",EDGE,{"derivedFrom":subQ3}),-1.0]])]});}
            var Q34;
            {var subQ4=sQuery(id+"F0.wireOp",EDGE,"E32");var subQ5=sQuery(id+"F0.wireOp",EDGE,"E28");var subQ6=makeQuery(id+"F0.imprint","INTERSECT",VERTEX,{"derivedFrom":[subQ5,subQ4]});Q34=makeQuery(id+"F0.imprint","IMPRINT",FACE,{"disambiguationData":[TD([[makeQuery(id+"F0.imprint","IMPRINT",EDGE,{"disambiguationData":[TD([[subQ6,1.0]])],"derivedFrom":subQ4}),1.0]])]});}
            var Q35;
            {var subQ0=sQuery(id+"F0.wireOp",EDGE,"E7");Q35=makeQuery(id+"F0.imprint","IMPRINT",FACE,{"disambiguationData":[TD([[makeQuery(id+"F0.imprint","IMPRINT",EDGE,{"derivedFrom":subQ0}),-1.0]])]});}
            var Q36;
            {var subQ5=sQuery(id+"F0.wireOp",EDGE,"E0");var subQ8=sQuery(id+"F0.wireOp",EDGE,"E30");var subQ9=makeQuery(id+"F0.imprint","INTERSECT",VERTEX,{"derivedFrom":[subQ5,subQ8]});Q36=makeQuery(id+"F0.imprint","IMPRINT",FACE,{"disambiguationData":[TD([[makeQuery(id+"F0.imprint","IMPRINT",EDGE,{"disambiguationData":[TD([[subQ9,-1.0]])],"derivedFrom":subQ5}),1.0]])]});}
            var Q37;
            {var subQ3=sQuery(id+"F0.wireOp",EDGE,"E34");Q37=makeQuery(id+"F0.imprint","IMPRINT",FACE,{"disambiguationData":[TD([[makeQuery(id+"F0.imprint","IMPRINT",EDGE,{"derivedFrom":subQ3}),1.0]])]});}
            var Q38;
            {var subQ1=sQuery(id+"F0.wireOp",EDGE,"E34");Q38=makeQuery(id+"F0.imprint","IMPRINT",FACE,{"disambiguationData":[TD([[makeQuery(id+"F0.imprint","IMPRINT",EDGE,{"derivedFrom":subQ1}),-1.0]])]});}
            var Q39;
            {var subQ6=sQuery(id+"F0.wireOp",EDGE,"E24");Q39=makeQuery(id+"F0.imprint","IMPRINT",FACE,{"disambiguationData":[TD([[makeQuery(id+"F0.imprint","IMPRINT",EDGE,{"derivedFrom":subQ6}),-1.0]])]});}
            var Q40;
            {var subQ3=sQuery(id+"F0.wireOp",EDGE,"E100");Q40=makeQuery(id+"F0.imprint","IMPRINT",FACE,{"disambiguationData":[TD([[makeQuery(id+"F0.imprint","IMPRINT",EDGE,{"derivedFrom":subQ3}),1.0]])]});}
            var Q41;
            {var subQ0=sQuery(id+"F0.wireOp",EDGE,"E16");var subQ1=makeQuery(id+"F0.imprint","IMPRINT",VERTEX,{"derivedFrom":subQ0});Q41=makeQuery(id+"F0.imprint","IMPRINT",FACE,{"disambiguationData":[TD([[makeQuery(id+"F0.imprint","IMPRINT",EDGE,{"disambiguationData":[TD([[subQ1,1.0]])],"derivedFrom":subQ0}),-1.0]])]});}
            var Q42;
            {var subQ0=sQuery(id+"F0.wireOp",EDGE,"E42");var subQ1=sQuery(id+"F0.wireOp",EDGE,"E33");var subQ2=makeQuery(id+"F0.imprint","INTERSECT",VERTEX,{"derivedFrom":[subQ1,subQ0]});Q42=makeQuery(id+"F0.imprint","IMPRINT",FACE,{"disambiguationData":[TD([[makeQuery(id+"F0.imprint","IMPRINT",EDGE,{"disambiguationData":[TD([[subQ2,-1.0]])],"derivedFrom":subQ1}),-1.0]])]});}
            var Q43;
            {var subQ0=sQuery(id+"F0.wireOp",EDGE,"E7");Q43=makeQuery(id+"F0.imprint","IMPRINT",FACE,{"disambiguationData":[TD([[makeQuery(id+"F0.imprint","IMPRINT",EDGE,{"derivedFrom":subQ0}),1.0]])]});}
            var Q44;
            {var subQ9=sQuery(id+"F0.wireOp",EDGE,"E21");Q44=makeQuery(id+"F0.imprint","IMPRINT",FACE,{"disambiguationData":[TD([[makeQuery(id+"F0.imprint","IMPRINT",EDGE,{"derivedFrom":subQ9}),1.0]])]});}
            var Q45;
            {var subQ0=sQuery(id+"F0.wireOp",EDGE,"E54");var subQ1=sQuery(id+"F0.wireOp",EDGE,"E46");var subQ2=makeQuery(id+"F0.imprint","INTERSECT",VERTEX,{"derivedFrom":[subQ1,subQ0]});Q45=makeQuery(id+"F0.imprint","IMPRINT",FACE,{"disambiguationData":[TD([[makeQuery(id+"F0.imprint","IMPRINT",EDGE,{"disambiguationData":[TD([[subQ2,-1.0]])],"derivedFrom":subQ1}),-1.0]])]});}
            var Q46;
            {var subQ0=sQuery(id+"F0.wireOp",EDGE,"E59");var subQ1=sQuery(id+"F0.wireOp",EDGE,"E46");var subQ2=makeQuery(id+"F0.imprint","INTERSECT",VERTEX,{"derivedFrom":[subQ1,subQ0]});Q46=makeQuery(id+"F0.imprint","IMPRINT",FACE,{"disambiguationData":[TD([[makeQuery(id+"F0.imprint","IMPRINT",EDGE,{"disambiguationData":[TD([[subQ2,-1.0]])],"derivedFrom":subQ1}),1.0]])]});}
            var Q47;
            {var subQ0=sQuery(id+"F0.wireOp",EDGE,"E56");var subQ1=sQuery(id+"F0.wireOp",EDGE,"E46");var subQ2=makeQuery(id+"F0.imprint","INTERSECT",VERTEX,{"derivedFrom":[subQ1,subQ0]});Q47=makeQuery(id+"F0.imprint","IMPRINT",FACE,{"disambiguationData":[TD([[makeQuery(id+"F0.imprint","IMPRINT",EDGE,{"disambiguationData":[TD([[subQ2,-1.0]])],"derivedFrom":subQ1}),1.0]])]});}
            var Q48;
            {var subQ0=sQuery(id+"F0.wireOp",EDGE,"E58");var subQ1=makeQuery(id+"F0.imprint","INTERSECT",VERTEX,{"derivedFrom":[subQ0,sQuery(id+"F0.wireOp",EDGE,"E59")]});Q48=makeQuery(id+"F0.imprint","IMPRINT",FACE,{"disambiguationData":[TD([[makeQuery(id+"F0.imprint","IMPRINT",EDGE,{"disambiguationData":[TD([[subQ1,-1.0]])],"derivedFrom":subQ0}),1.0]])]});}
            var Q49;
            {var subQ0=sQuery(id+"F0.wireOp",EDGE,"E56");var subQ1=sQuery(id+"F0.wireOp",EDGE,"E46");var subQ2=makeQuery(id+"F0.imprint","INTERSECT",VERTEX,{"derivedFrom":[subQ1,subQ0]});Q49=makeQuery(id+"F0.imprint","IMPRINT",FACE,{"disambiguationData":[TD([[makeQuery(id+"F0.imprint","IMPRINT",EDGE,{"disambiguationData":[TD([[subQ2,-1.0]])],"derivedFrom":subQ1}),-1.0]])]});}
            var Q50;
            {var subQ0=sQuery(id+"F0.wireOp",EDGE,"E59");var subQ1=sQuery(id+"F0.wireOp",EDGE,"E46");var subQ2=makeQuery(id+"F0.imprint","INTERSECT",VERTEX,{"derivedFrom":[subQ1,subQ0]});Q50=makeQuery(id+"F0.imprint","IMPRINT",FACE,{"disambiguationData":[TD([[makeQuery(id+"F0.imprint","IMPRINT",EDGE,{"disambiguationData":[TD([[subQ2,-1.0]])],"derivedFrom":subQ1}),-1.0]])]});}
            var Q51;
            {var subQ5=sQuery(id+"F0.wireOp",EDGE,"E47");var subQ6=sQuery(id+"F0.wireOp",EDGE,"E6");var subQ7=makeQuery(id+"F0.imprint","INTERSECT",VERTEX,{"derivedFrom":[subQ6,subQ5]});Q51=makeQuery(id+"F0.imprint","IMPRINT",FACE,{"disambiguationData":[TD([[makeQuery(id+"F0.imprint","IMPRINT",EDGE,{"disambiguationData":[TD([[subQ7,1.0]])],"derivedFrom":subQ6}),-1.0]])]});}
            var Q52;
            {var subQ4=sQuery(id+"F0.wireOp",EDGE,"E49");Q52=makeQuery(id+"F0.imprint","IMPRINT",FACE,{"disambiguationData":[TD([[makeQuery(id+"F0.imprint","IMPRINT",EDGE,{"derivedFrom":subQ4}),-1.0]])]});}
            var Q53;
            {var subQ0=sQuery(id+"F0.wireOp",EDGE,"E83");var subQ1=sQuery(id+"F0.wireOp",EDGE,"E82");var subQ2=makeQuery(id+"F0.imprint","INTERSECT",VERTEX,{"derivedFrom":[subQ1,subQ0]});Q53=makeQuery(id+"F0.imprint","IMPRINT",FACE,{"disambiguationData":[TD([[makeQuery(id+"F0.imprint","IMPRINT",EDGE,{"disambiguationData":[TD([[subQ2,-1.0]])],"derivedFrom":subQ1}),-1.0]])]});}
            var Q54;
            {var subQ1=sQuery(id+"F0.wireOp",EDGE,"E80");var subQ5=sQuery(id+"F0.wireOp",EDGE,"E79");var subQ6=makeQuery(id+"F0.imprint","INTERSECT",VERTEX,{"derivedFrom":[subQ5,subQ1]});Q54=makeQuery(id+"F0.imprint","IMPRINT",FACE,{"disambiguationData":[TD([[makeQuery(id+"F0.imprint","IMPRINT",EDGE,{"disambiguationData":[TD([[subQ6,1.0]])],"derivedFrom":subQ5}),1.0]])]});}
            var Q55;
            {var subQ0=sQuery(id+"F0.wireOp",EDGE,"E85");var subQ4=makeQuery(id+"F0.imprint","INTERSECT",VERTEX,{"derivedFrom":[sQuery(id+"F0.wireOp",EDGE,"E82"),subQ0]});Q55=makeQuery(id+"F0.imprint","IMPRINT",FACE,{"disambiguationData":[TD([[makeQuery(id+"F0.imprint","IMPRINT",EDGE,{"disambiguationData":[TD([[subQ4,1.0]])],"derivedFrom":subQ0}),1.0]])]});}
            var Q56;
            {var subQ0=sQuery(id+"F0.wireOp",EDGE,"E85");var subQ1=sQuery(id+"F0.wireOp",EDGE,"E82");var subQ2=makeQuery(id+"F0.imprint","INTERSECT",VERTEX,{"derivedFrom":[subQ1,subQ0]});Q56=makeQuery(id+"F0.imprint","IMPRINT",FACE,{"disambiguationData":[TD([[makeQuery(id+"F0.imprint","IMPRINT",EDGE,{"disambiguationData":[TD([[subQ2,1.0]])],"derivedFrom":subQ1}),1.0]])]});}
            var Q57;
            {var subQ0=sQuery(id+"F0.wireOp",EDGE,"E85");var subQ1=sQuery(id+"F0.wireOp",EDGE,"E82");var subQ2=makeQuery(id+"F0.imprint","INTERSECT",VERTEX,{"derivedFrom":[subQ1,subQ0]});Q57=makeQuery(id+"F0.imprint","IMPRINT",FACE,{"disambiguationData":[TD([[makeQuery(id+"F0.imprint","IMPRINT",EDGE,{"disambiguationData":[TD([[subQ2,1.0]])],"derivedFrom":subQ1}),-1.0]])]});}
            var Q58;
            {var subQ0=sQuery(id+"F0.wireOp",EDGE,"E80");var subQ1=sQuery(id+"F0.wireOp",EDGE,"E79");var subQ2=makeQuery(id+"F0.imprint","INTERSECT",VERTEX,{"derivedFrom":[subQ1,subQ0]});Q58=makeQuery(id+"F0.imprint","IMPRINT",FACE,{"disambiguationData":[TD([[makeQuery(id+"F0.imprint","IMPRINT",EDGE,{"disambiguationData":[TD([[subQ2,1.0]])],"derivedFrom":subQ1}),-1.0]])]});}
            var Q59;
            {var subQ0=sQuery(id+"F0.wireOp",EDGE,"E3");var subQ1=sQuery(id+"F0.wireOp",EDGE,"E0");var subQ2=makeQuery(id+"F0.imprint","INTERSECT",VERTEX,{"derivedFrom":[subQ1,subQ0]});Q59=makeQuery(id+"F0.imprint","IMPRINT",FACE,{"disambiguationData":[TD([[makeQuery(id+"F0.imprint","IMPRINT",EDGE,{"disambiguationData":[TD([[subQ2,-1.0]])],"derivedFrom":subQ1}),1.0]])]});}
            var Q60;
            {var subQ6=sQuery(id+"F0.wireOp",EDGE,"E28");var subQ9=sQuery(id+"F0.wireOp",EDGE,"E75");var subQ10=makeQuery(id+"F0.imprint","INTERSECT",VERTEX,{"derivedFrom":[subQ6,subQ9]});Q60=makeQuery(id+"F0.imprint","IMPRINT",FACE,{"disambiguationData":[TD([[makeQuery(id+"F0.imprint","IMPRINT",EDGE,{"disambiguationData":[TD([[subQ10,-1.0]])],"derivedFrom":subQ6}),1.0]])]});}
            var Q61;
            {var subQ0=sQuery(id+"F0.wireOp",EDGE,"E77");var subQ1=sQuery(id+"F0.wireOp",EDGE,"E28");var subQ2=makeQuery(id+"F0.imprint","INTERSECT",VERTEX,{"derivedFrom":[subQ1,subQ0]});Q61=makeQuery(id+"F0.imprint","IMPRINT",FACE,{"disambiguationData":[TD([[makeQuery(id+"F0.imprint","IMPRINT",EDGE,{"disambiguationData":[TD([[subQ2,-1.0]])],"derivedFrom":subQ1}),-1.0]])]});}
            var Q62;
            {var subQ0=sQuery(id+"F0.wireOp",EDGE,"E72");var subQ1=sQuery(id+"F0.wireOp",EDGE,"E28");var subQ2=makeQuery(id+"F0.imprint","INTERSECT",VERTEX,{"derivedFrom":[subQ1,subQ0]});Q62=makeQuery(id+"F0.imprint","IMPRINT",FACE,{"disambiguationData":[TD([[makeQuery(id+"F0.imprint","IMPRINT",EDGE,{"disambiguationData":[TD([[subQ2,-1.0]])],"derivedFrom":subQ1}),-1.0]])]});}
            var Q63;
            {var subQ0=sQuery(id+"F0.wireOp",EDGE,"E77");var subQ1=sQuery(id+"F0.wireOp",EDGE,"E28");var subQ2=makeQuery(id+"F0.imprint","INTERSECT",VERTEX,{"derivedFrom":[subQ1,subQ0]});Q63=makeQuery(id+"F0.imprint","IMPRINT",FACE,{"disambiguationData":[TD([[makeQuery(id+"F0.imprint","IMPRINT",EDGE,{"disambiguationData":[TD([[subQ2,-1.0]])],"derivedFrom":subQ1}),1.0]])]});}
            var Q64;
            {var subQ0=sQuery(id+"F0.wireOp",EDGE,"E72");var subQ1=sQuery(id+"F0.wireOp",EDGE,"E28");var subQ2=makeQuery(id+"F0.imprint","INTERSECT",VERTEX,{"derivedFrom":[subQ1,subQ0]});Q64=makeQuery(id+"F0.imprint","IMPRINT",FACE,{"disambiguationData":[TD([[makeQuery(id+"F0.imprint","IMPRINT",EDGE,{"disambiguationData":[TD([[subQ2,-1.0]])],"derivedFrom":subQ1}),1.0]])]});}
            var Q65;
            {var subQ0=sQuery(id+"F0.wireOp",EDGE,"E76");var subQ1=sQuery(id+"F0.wireOp",EDGE,"E72");var subQ2=makeQuery(id+"F0.imprint","INTERSECT",VERTEX,{"derivedFrom":[subQ1,subQ0]});Q65=makeQuery(id+"F0.imprint","IMPRINT",FACE,{"disambiguationData":[TD([[makeQuery(id+"F0.imprint","IMPRINT",EDGE,{"disambiguationData":[TD([[subQ2,-1.0]])],"derivedFrom":subQ1}),1.0]])]});}
            var Q66;
            {var subQ0=sQuery(id+"F0.wireOp",EDGE,"E76");var subQ1=sQuery(id+"F0.wireOp",EDGE,"E72");var subQ2=makeQuery(id+"F0.imprint","INTERSECT",VERTEX,{"derivedFrom":[subQ1,subQ0]});Q66=makeQuery(id+"F0.imprint","IMPRINT",FACE,{"disambiguationData":[TD([[makeQuery(id+"F0.imprint","IMPRINT",EDGE,{"disambiguationData":[TD([[subQ2,-1.0]])],"derivedFrom":subQ1}),-1.0]])]});}
            var Q67;
            {var subQ0=sQuery(id+"F0.wireOp",EDGE,"E76");var subQ4=makeQuery(id+"F0.imprint","INTERSECT",VERTEX,{"derivedFrom":[sQuery(id+"F0.wireOp",EDGE,"E72"),subQ0]});Q67=makeQuery(id+"F0.imprint","IMPRINT",FACE,{"disambiguationData":[TD([[makeQuery(id+"F0.imprint","IMPRINT",EDGE,{"disambiguationData":[TD([[subQ4,1.0]])],"derivedFrom":subQ0}),-1.0]])]});}
            var Q68;
            {var subQ0=sQuery(id+"F0.wireOp",EDGE,"E74");var subQ1=makeQuery(id+"F0.imprint","INTERSECT",VERTEX,{"derivedFrom":[sQuery(id+"F0.wireOp",EDGE,"E72"),subQ0]});Q68=makeQuery(id+"F0.imprint","IMPRINT",FACE,{"disambiguationData":[TD([[makeQuery(id+"F0.imprint","IMPRINT",EDGE,{"disambiguationData":[TD([[subQ1,1.0]])],"derivedFrom":subQ0}),1.0]])]});}
            var Q69;
            {var subQ1=sQuery(id+"F0.wireOp",EDGE,"E64");var subQ5=sQuery(id+"F0.wireOp",EDGE,"E63");var subQ6=makeQuery(id+"F0.imprint","INTERSECT",VERTEX,{"derivedFrom":[subQ5,subQ1]});Q69=makeQuery(id+"F0.imprint","IMPRINT",FACE,{"disambiguationData":[TD([[makeQuery(id+"F0.imprint","IMPRINT",EDGE,{"disambiguationData":[TD([[subQ6,1.0]])],"derivedFrom":subQ5}),1.0]])]});}
            var Q70;
            {var subQ0=sQuery(id+"F0.wireOp",EDGE,"E30");var subQ1=sQuery(id+"F0.wireOp",EDGE,"E28");var subQ2=makeQuery(id+"F0.imprint","INTERSECT",VERTEX,{"derivedFrom":[subQ1,subQ0]});Q70=makeQuery(id+"F0.imprint","IMPRINT",FACE,{"disambiguationData":[TD([[makeQuery(id+"F0.imprint","IMPRINT",EDGE,{"disambiguationData":[TD([[subQ2,1.0]])],"derivedFrom":subQ1}),-1.0]])]});}
            var Q71;
            {var subQ0=sQuery(id+"F0.wireOp",EDGE,"E68");var subQ1=sQuery(id+"F0.wireOp",EDGE,"E30");var subQ2=makeQuery(id+"F0.imprint","INTERSECT",VERTEX,{"disambiguationData":[OD(0.0)],"derivedFrom":[subQ1,subQ0]});Q71=makeQuery(id+"F0.imprint","IMPRINT",FACE,{"disambiguationData":[TD([[makeQuery(id+"F0.imprint","IMPRINT",EDGE,{"disambiguationData":[TD([[subQ2,-1.0]])],"derivedFrom":subQ1}),-1.0]])]});}
            var Q72;
            {var subQ0=sQuery(id+"F0.wireOp",EDGE,"E69");var subQ1=sQuery(id+"F0.wireOp",EDGE,"E66");var subQ2=makeQuery(id+"F0.imprint","INTERSECT",VERTEX,{"derivedFrom":[subQ1,subQ0]});Q72=makeQuery(id+"F0.imprint","IMPRINT",FACE,{"disambiguationData":[TD([[makeQuery(id+"F0.imprint","IMPRINT",EDGE,{"disambiguationData":[TD([[subQ2,1.0]])],"derivedFrom":subQ1}),1.0]])]});}
            var Q73;
            {var subQ0=sQuery(id+"F0.wireOp",EDGE,"E69");var subQ1=sQuery(id+"F0.wireOp",EDGE,"E30");var subQ2=makeQuery(id+"F0.imprint","INTERSECT",VERTEX,{"derivedFrom":[subQ1,subQ0]});Q73=makeQuery(id+"F0.imprint","IMPRINT",FACE,{"disambiguationData":[TD([[makeQuery(id+"F0.imprint","IMPRINT",EDGE,{"disambiguationData":[TD([[subQ2,-1.0]])],"derivedFrom":subQ1}),1.0]])]});}
            var Q74;
            {var subQ0=sQuery(id+"F0.wireOp",EDGE,"E30");var subQ8=sQuery(id+"F0.wireOp",EDGE,"E29");var subQ9=makeQuery(id+"F0.imprint","INTERSECT",VERTEX,{"derivedFrom":[subQ8,subQ0]});Q74=makeQuery(id+"F0.imprint","IMPRINT",FACE,{"disambiguationData":[TD([[makeQuery(id+"F0.imprint","IMPRINT",EDGE,{"disambiguationData":[TD([[subQ9,1.0]])],"derivedFrom":subQ8}),1.0]])]});}
            var Q75;
            {var subQ0=sQuery(id+"F0.wireOp",EDGE,"E69");var subQ1=sQuery(id+"F0.wireOp",EDGE,"E30");var subQ2=makeQuery(id+"F0.imprint","INTERSECT",VERTEX,{"derivedFrom":[subQ1,subQ0]});Q75=makeQuery(id+"F0.imprint","IMPRINT",FACE,{"disambiguationData":[TD([[makeQuery(id+"F0.imprint","IMPRINT",EDGE,{"disambiguationData":[TD([[subQ2,-1.0]])],"derivedFrom":subQ1}),-1.0]])]});}
            var Q76;
            {var subQ0=sQuery(id+"F0.wireOp",EDGE,"E68");var subQ1=sQuery(id+"F0.wireOp",EDGE,"E30");var subQ2=makeQuery(id+"F0.imprint","INTERSECT",VERTEX,{"disambiguationData":[OD(0.0)],"derivedFrom":[subQ1,subQ0]});Q76=makeQuery(id+"F0.imprint","IMPRINT",FACE,{"disambiguationData":[TD([[makeQuery(id+"F0.imprint","IMPRINT",EDGE,{"disambiguationData":[TD([[subQ2,-1.0]])],"derivedFrom":subQ1}),1.0]])]});}
            var Q77;
            {var subQ0=sQuery(id+"F0.wireOp",EDGE,"E65");Q77=makeQuery(id+"F0.imprint","IMPRINT",FACE,{"disambiguationData":[TD([[makeQuery(id+"F0.imprint","IMPRINT",EDGE,{"derivedFrom":subQ0}),-1.0]])]});}
            var Q78;
            {var subQ0=sQuery(id+"F0.wireOp",EDGE,"E67");var subQ1=sQuery(id+"F0.wireOp",EDGE,"E0");var subQ2=makeQuery(id+"F0.imprint","INTERSECT",VERTEX,{"derivedFrom":[subQ1,subQ0]});Q78=makeQuery(id+"F0.imprint","IMPRINT",FACE,{"disambiguationData":[TD([[makeQuery(id+"F0.imprint","IMPRINT",EDGE,{"disambiguationData":[TD([[subQ2,-1.0]])],"derivedFrom":subQ1}),-1.0]])]});}
            var Q79;
            {var subQ0=sQuery(id+"F0.wireOp",EDGE,"E29");var subQ1=sQuery(id+"F0.wireOp",EDGE,"E0");var subQ2=makeQuery(id+"F0.imprint","INTERSECT",VERTEX,{"derivedFrom":[subQ1,subQ0]});Q79=makeQuery(id+"F0.imprint","IMPRINT",FACE,{"disambiguationData":[TD([[makeQuery(id+"F0.imprint","IMPRINT",EDGE,{"disambiguationData":[TD([[subQ2,1.0]])],"derivedFrom":subQ1}),-1.0]])]});}
            var Q80;
            {var subQ0=sQuery(id+"F0.wireOp",EDGE,"E30");var subQ1=sQuery(id+"F0.wireOp",EDGE,"E28");var subQ2=makeQuery(id+"F0.imprint","INTERSECT",VERTEX,{"derivedFrom":[subQ1,subQ0]});Q80=makeQuery(id+"F0.imprint","IMPRINT",FACE,{"disambiguationData":[TD([[makeQuery(id+"F0.imprint","IMPRINT",EDGE,{"disambiguationData":[TD([[subQ2,1.0]])],"derivedFrom":subQ1}),1.0]])]});}
            var Q81;
            {var subQ0=sQuery(id+"F0.wireOp",EDGE,"E65");Q81=makeQuery(id+"F0.imprint","IMPRINT",FACE,{"disambiguationData":[TD([[makeQuery(id+"F0.imprint","IMPRINT",EDGE,{"derivedFrom":subQ0}),1.0]])]});}
            var Q82;
            {var subQ5=sQuery(id+"F0.wireOp",EDGE,"E29");var subQ7=sQuery(id+"F0.wireOp",EDGE,"E0");var subQ8=makeQuery(id+"F0.imprint","INTERSECT",VERTEX,{"derivedFrom":[subQ7,subQ5]});Q82=makeQuery(id+"F0.imprint","IMPRINT",FACE,{"disambiguationData":[TD([[makeQuery(id+"F0.imprint","IMPRINT",EDGE,{"disambiguationData":[TD([[subQ8,1.0]])],"derivedFrom":subQ7}),1.0]])]});}
            var Q83;
            {var subQ0=sQuery(id+"F0.wireOp",EDGE,"E64");var subQ1=sQuery(id+"F0.wireOp",EDGE,"E63");var subQ2=makeQuery(id+"F0.imprint","INTERSECT",VERTEX,{"derivedFrom":[subQ1,subQ0]});Q83=makeQuery(id+"F0.imprint","IMPRINT",FACE,{"disambiguationData":[TD([[makeQuery(id+"F0.imprint","IMPRINT",EDGE,{"disambiguationData":[TD([[subQ2,1.0]])],"derivedFrom":subQ1}),-1.0]])]});}
            var Q84;
            {var subQ4=sQuery(id+"F0.wireOp",EDGE,"E81");Q84=makeQuery(id+"F0.imprint","IMPRINT",FACE,{"disambiguationData":[TD([[makeQuery(id+"F0.imprint","IMPRINT",EDGE,{"derivedFrom":subQ4}),-1.0]])]});}
            var Q85;
            {var subQ1=sQuery(id+"F0.wireOp",EDGE,"E82");var subQ3=sQuery(id+"F0.wireOp",EDGE,"E83");var subQ4=makeQuery(id+"F0.imprint","INTERSECT",VERTEX,{"derivedFrom":[subQ1,subQ3]});Q85=makeQuery(id+"F0.imprint","IMPRINT",FACE,{"disambiguationData":[TD([[makeQuery(id+"F0.imprint","IMPRINT",EDGE,{"disambiguationData":[TD([[subQ4,1.0]])],"derivedFrom":subQ3}),1.0]])]});}
            var Q86;
            {var subQ0=sQuery(id+"F0.wireOp",EDGE,"E81");Q86=makeQuery(id+"F0.imprint","IMPRINT",FACE,{"disambiguationData":[TD([[makeQuery(id+"F0.imprint","IMPRINT",EDGE,{"derivedFrom":subQ0}),1.0]])]});}
            var Q87;
            {var subQ0=sQuery(id+"F0.wireOp",EDGE,"E90");var subQ1=sQuery(id+"F0.wireOp",EDGE,"E88");var subQ2=makeQuery(id+"F0.imprint","INTERSECT",VERTEX,{"derivedFrom":[subQ1,subQ0]});Q87=makeQuery(id+"F0.imprint","IMPRINT",FACE,{"disambiguationData":[TD([[makeQuery(id+"F0.imprint","IMPRINT",EDGE,{"disambiguationData":[TD([[subQ2,1.0]])],"derivedFrom":subQ1}),1.0]])]});}
            var Q88;
            {var subQ5=sQuery(id+"F0.wireOp",EDGE,"E93");Q88=makeQuery(id+"F0.imprint","IMPRINT",FACE,{"disambiguationData":[TD([[makeQuery(id+"F0.imprint","IMPRINT",EDGE,{"derivedFrom":subQ5}),1.0]])]});}
            var Q89;
            {var subQ0=sQuery(id+"F0.wireOp",EDGE,"E92");var subQ1=sQuery(id+"F0.wireOp",EDGE,"E88");var subQ2=makeQuery(id+"F0.imprint","INTERSECT",VERTEX,{"derivedFrom":[subQ1,subQ0]});Q89=makeQuery(id+"F0.imprint","IMPRINT",FACE,{"disambiguationData":[TD([[makeQuery(id+"F0.imprint","IMPRINT",EDGE,{"disambiguationData":[TD([[subQ2,-1.0]])],"derivedFrom":subQ1}),-1.0]])]});}
            var Q90;
            {var subQ0=sQuery(id+"F0.wireOp",EDGE,"E92");var subQ1=sQuery(id+"F0.wireOp",EDGE,"E89");var subQ2=makeQuery(id+"F0.imprint","INTERSECT",VERTEX,{"derivedFrom":[subQ1,subQ0]});Q90=makeQuery(id+"F0.imprint","IMPRINT",FACE,{"disambiguationData":[TD([[makeQuery(id+"F0.imprint","IMPRINT",EDGE,{"disambiguationData":[TD([[subQ2,-1.0]])],"derivedFrom":subQ0}),-1.0]])]});}
            var Q91;
            {var subQ0=sQuery(id+"F0.wireOp",EDGE,"E92");var subQ1=sQuery(id+"F0.wireOp",EDGE,"E88");var subQ2=makeQuery(id+"F0.imprint","INTERSECT",VERTEX,{"derivedFrom":[subQ1,subQ0]});Q91=makeQuery(id+"F0.imprint","IMPRINT",FACE,{"disambiguationData":[TD([[makeQuery(id+"F0.imprint","IMPRINT",EDGE,{"disambiguationData":[TD([[subQ2,-1.0]])],"derivedFrom":subQ1}),1.0]])]});}
            var Q92;
            {var subQ0=sQuery(id+"F0.wireOp",EDGE,"E90");var subQ1=makeQuery(id+"F0.imprint","INTERSECT",VERTEX,{"derivedFrom":[sQuery(id+"F0.wireOp",EDGE,"E88"),subQ0]});Q92=makeQuery(id+"F0.imprint","IMPRINT",FACE,{"disambiguationData":[TD([[makeQuery(id+"F0.imprint","IMPRINT",EDGE,{"disambiguationData":[TD([[subQ1,1.0]])],"derivedFrom":subQ0}),1.0]])]});}
            var Q93;
            {var subQ4=sQuery(id+"F0.wireOp",EDGE,"E46");var subQ6=sQuery(id+"F0.wireOp",EDGE,"E50");var subQ7=makeQuery(id+"F0.imprint","INTERSECT",VERTEX,{"derivedFrom":[subQ4,subQ6]});Q93=makeQuery(id+"F0.imprint","IMPRINT",FACE,{"disambiguationData":[TD([[makeQuery(id+"F0.imprint","IMPRINT",EDGE,{"disambiguationData":[TD([[subQ7,-1.0]])],"derivedFrom":subQ4}),-1.0]])]});}
            var Q94;
            {var subQ0=sQuery(id+"F0.wireOp",EDGE,"E51");var subQ1=sQuery(id+"F0.wireOp",EDGE,"E27");var subQ2=makeQuery(id+"F0.imprint","INTERSECT",VERTEX,{"disambiguationData":[OD(0.0)],"derivedFrom":[subQ1,subQ0]});Q94=makeQuery(id+"F0.imprint","IMPRINT",FACE,{"disambiguationData":[TD([[makeQuery(id+"F0.imprint","IMPRINT",EDGE,{"disambiguationData":[TD([[subQ2,-1.0]])],"derivedFrom":subQ1}),1.0]])]});}
            var Q95;
            {var subQ0=sQuery(id+"F0.wireOp",EDGE,"E55");var subQ1=sQuery(id+"F0.wireOp",EDGE,"E27");var subQ2=makeQuery(id+"F0.imprint","INTERSECT",VERTEX,{"derivedFrom":[subQ1,subQ0]});Q95=makeQuery(id+"F0.imprint","IMPRINT",FACE,{"disambiguationData":[TD([[makeQuery(id+"F0.imprint","IMPRINT",EDGE,{"disambiguationData":[TD([[subQ2,-1.0]])],"derivedFrom":subQ1}),1.0]])]});}
            var Q96;
            {var subQ0=sQuery(id+"F0.wireOp",EDGE,"E49");Q96=makeQuery(id+"F0.imprint","IMPRINT",FACE,{"disambiguationData":[TD([[makeQuery(id+"F0.imprint","IMPRINT",EDGE,{"derivedFrom":subQ0}),1.0]])]});}
            var Q97;
            {var subQ0=sQuery(id+"F0.wireOp",EDGE,"E53");var subQ4=makeQuery(id+"F0.imprint","INTERSECT",VERTEX,{"derivedFrom":[sQuery(id+"F0.wireOp",EDGE,"E50"),subQ0]});Q97=makeQuery(id+"F0.imprint","IMPRINT",FACE,{"disambiguationData":[TD([[makeQuery(id+"F0.imprint","IMPRINT",EDGE,{"disambiguationData":[TD([[subQ4,1.0]])],"derivedFrom":subQ0}),1.0]])]});}
            var Q98;
            {var subQ0=sQuery(id+"F0.wireOp",EDGE,"E53");var subQ1=sQuery(id+"F0.wireOp",EDGE,"E50");var subQ2=makeQuery(id+"F0.imprint","INTERSECT",VERTEX,{"derivedFrom":[subQ1,subQ0]});Q98=makeQuery(id+"F0.imprint","IMPRINT",FACE,{"disambiguationData":[TD([[makeQuery(id+"F0.imprint","IMPRINT",EDGE,{"disambiguationData":[TD([[subQ2,1.0]])],"derivedFrom":subQ1}),1.0]])]});}
            var Q99;
            {var subQ0=sQuery(id+"F0.wireOp",EDGE,"E53");var subQ1=sQuery(id+"F0.wireOp",EDGE,"E50");var subQ2=makeQuery(id+"F0.imprint","INTERSECT",VERTEX,{"derivedFrom":[subQ1,subQ0]});Q99=makeQuery(id+"F0.imprint","IMPRINT",FACE,{"disambiguationData":[TD([[makeQuery(id+"F0.imprint","IMPRINT",EDGE,{"disambiguationData":[TD([[subQ2,1.0]])],"derivedFrom":subQ1}),-1.0]])]});}
            var Q100;
            {var subQ0=sQuery(id+"F0.wireOp",EDGE,"E50");var subQ1=sQuery(id+"F0.wireOp",EDGE,"E46");var subQ2=makeQuery(id+"F0.imprint","INTERSECT",VERTEX,{"derivedFrom":[subQ1,subQ0]});Q100=makeQuery(id+"F0.imprint","IMPRINT",FACE,{"disambiguationData":[TD([[makeQuery(id+"F0.imprint","IMPRINT",EDGE,{"disambiguationData":[TD([[subQ2,-1.0]])],"derivedFrom":subQ1}),1.0]])]});}
            var Q101;
            {var subQ0=sQuery(id+"F0.wireOp",EDGE,"E60");var subQ4=makeQuery(id+"F0.imprint","INTERSECT",VERTEX,{"derivedFrom":[sQuery(id+"F0.wireOp",EDGE,"E56"),subQ0]});Q101=makeQuery(id+"F0.imprint","IMPRINT",FACE,{"disambiguationData":[TD([[makeQuery(id+"F0.imprint","IMPRINT",EDGE,{"disambiguationData":[TD([[subQ4,-1.0]])],"derivedFrom":subQ0}),-1.0]])]});}
            var Q102;
            {var subQ0=sQuery(id+"F0.wireOp",EDGE,"E60");var subQ1=sQuery(id+"F0.wireOp",EDGE,"E56");var subQ2=makeQuery(id+"F0.imprint","INTERSECT",VERTEX,{"derivedFrom":[subQ1,subQ0]});Q102=makeQuery(id+"F0.imprint","IMPRINT",FACE,{"disambiguationData":[TD([[makeQuery(id+"F0.imprint","IMPRINT",EDGE,{"disambiguationData":[TD([[subQ2,-1.0]])],"derivedFrom":subQ1}),1.0]])]});}
            var Q103;
            {var subQ0=sQuery(id+"F0.wireOp",EDGE,"E60");var subQ1=sQuery(id+"F0.wireOp",EDGE,"E56");var subQ2=makeQuery(id+"F0.imprint","INTERSECT",VERTEX,{"derivedFrom":[subQ1,subQ0]});Q103=makeQuery(id+"F0.imprint","IMPRINT",FACE,{"disambiguationData":[TD([[makeQuery(id+"F0.imprint","IMPRINT",EDGE,{"disambiguationData":[TD([[subQ2,-1.0]])],"derivedFrom":subQ1}),-1.0]])]});}
            var Q104;
            {var subQ3=sQuery(id+"F0.wireOp",EDGE,"E50");var subQ5=sQuery(id+"F0.wireOp",EDGE,"E46");var subQ6=makeQuery(id+"F0.imprint","INTERSECT",VERTEX,{"derivedFrom":[subQ5,subQ3]});Q104=makeQuery(id+"F0.imprint","IMPRINT",FACE,{"disambiguationData":[TD([[makeQuery(id+"F0.imprint","IMPRINT",EDGE,{"disambiguationData":[TD([[subQ6,-1.0]])],"derivedFrom":subQ3}),1.0]])]});}
            var Q105;
            {var subQ3=sQuery(id+"F0.wireOp",EDGE,"E62");var subQ5=sQuery(id+"F0.wireOp",EDGE,"E51");var subQ7=makeQuery(id+"F0.imprint","INTERSECT",VERTEX,{"derivedFrom":[subQ5,subQ3]});Q105=makeQuery(id+"F0.imprint","IMPRINT",FACE,{"disambiguationData":[TD([[makeQuery(id+"F0.imprint","IMPRINT",EDGE,{"disambiguationData":[TD([[subQ7,1.0]])],"derivedFrom":subQ5}),-1.0]])]});}
            var Q106;
            {var subQ1=sQuery(id+"F0.wireOp",EDGE,"E46");var subQ3=sQuery(id+"F0.wireOp",EDGE,"E50");var subQ4=makeQuery(id+"F0.imprint","INTERSECT",VERTEX,{"derivedFrom":[subQ1,subQ3]});Q106=makeQuery(id+"F0.imprint","IMPRINT",FACE,{"disambiguationData":[TD([[makeQuery(id+"F0.imprint","IMPRINT",EDGE,{"disambiguationData":[TD([[subQ4,1.0]])],"derivedFrom":subQ3}),1.0]])]});}
            var Q107;
            {var subQ0=sQuery(id+"F0.wireOp",EDGE,"E51");var subQ1=sQuery(id+"F0.wireOp",EDGE,"E27");var subQ2=makeQuery(id+"F0.imprint","INTERSECT",VERTEX,{"disambiguationData":[OD(0.0)],"derivedFrom":[subQ1,subQ0]});Q107=makeQuery(id+"F0.imprint","IMPRINT",FACE,{"disambiguationData":[TD([[makeQuery(id+"F0.imprint","IMPRINT",EDGE,{"disambiguationData":[TD([[subQ2,-1.0]])],"derivedFrom":subQ1}),-1.0]])]});}
            var Q108;
            {var subQ0=sQuery(id+"F0.wireOp",EDGE,"E45");var subQ1=sQuery(id+"F0.wireOp",EDGE,"E35");var subQ2=makeQuery(id+"F0.imprint","INTERSECT",VERTEX,{"derivedFrom":[subQ1,subQ0]});Q108=makeQuery(id+"F0.imprint","IMPRINT",FACE,{"disambiguationData":[TD([[makeQuery(id+"F0.imprint","IMPRINT",EDGE,{"disambiguationData":[TD([[subQ2,-1.0]])],"derivedFrom":subQ1}),1.0]])]});}
            var Q109;
            {var subQ0=sQuery(id+"F0.wireOp",EDGE,"E132");Q109=makeQuery(id+"F0.imprint","IMPRINT",FACE,{"disambiguationData":[TD([[makeQuery(id+"F0.imprint","IMPRINT",EDGE,{"derivedFrom":subQ0}),1.0]])]});}
            var Q110;
            {var subQ0=sQuery(id+"F0.wireOp",EDGE,"E135");Q110=makeQuery(id+"F0.imprint","IMPRINT",FACE,{"disambiguationData":[TD([[makeQuery(id+"F0.imprint","IMPRINT",EDGE,{"derivedFrom":subQ0}),-1.0]])]});}
            var Q111;
            {var subQ1=sQuery(id+"F0.wireOp",EDGE,"E110");Q111=makeQuery(id+"F0.imprint","IMPRINT",FACE,{"disambiguationData":[TD([[makeQuery(id+"F0.imprint","IMPRINT",EDGE,{"derivedFrom":subQ1}),1.0]])]});}
            var Q112;
            {var subQ0=sQuery(id+"F0.wireOp",EDGE,"E112");Q112=makeQuery(id+"F0.imprint","IMPRINT",FACE,{"disambiguationData":[TD([[makeQuery(id+"F0.imprint","IMPRINT",EDGE,{"derivedFrom":subQ0}),-1.0]])]});}
            var Q113;
            {var subQ0=sQuery(id+"F0.wireOp",EDGE,"E110");Q113=makeQuery(id+"F0.imprint","IMPRINT",FACE,{"disambiguationData":[TD([[makeQuery(id+"F0.imprint","IMPRINT",EDGE,{"derivedFrom":subQ0}),-1.0]])]});}
            var Q114;
            {var subQ11=sQuery(id+"F0.wireOp",EDGE,"E100");Q114=makeQuery(id+"F0.imprint","IMPRINT",FACE,{"disambiguationData":[TD([[makeQuery(id+"F0.imprint","IMPRINT",EDGE,{"derivedFrom":subQ11}),-1.0]])]});}
            var Q115;
            {var subQ1=sQuery(id+"F0.wireOp",EDGE,"E21");Q115=makeQuery(id+"F0.imprint","IMPRINT",FACE,{"disambiguationData":[TD([[makeQuery(id+"F0.imprint","IMPRINT",EDGE,{"derivedFrom":subQ1}),-1.0]])]});}
            var Q116;
            {var subQ12=sQuery(id+"F0.wireOp",EDGE,"E104");Q116=makeQuery(id+"F0.imprint","IMPRINT",FACE,{"disambiguationData":[TD([[makeQuery(id+"F0.imprint","IMPRINT",EDGE,{"derivedFrom":subQ12}),1.0]])]});}
            var Q117;
            {var subQ1=sQuery(id+"F0.wireOp",EDGE,"E33");var subQ3=sQuery(id+"F0.wireOp",EDGE,"E161");var subQ4=makeQuery(id+"F0.imprint","INTERSECT",VERTEX,{"derivedFrom":[subQ1,subQ3]});Q117=makeQuery(id+"F0.imprint","IMPRINT",FACE,{"disambiguationData":[TD([[makeQuery(id+"F0.imprint","IMPRINT",EDGE,{"disambiguationData":[TD([[subQ4,-1.0]])],"derivedFrom":subQ3}),1.0]])]});}
            var Q118;
            {var subQ1=sQuery(id+"F0.wireOp",EDGE,"E35");var subQ3=sQuery(id+"F0.wireOp",EDGE,"E161");var subQ4=makeQuery(id+"F0.imprint","INTERSECT",VERTEX,{"derivedFrom":[subQ1,subQ3]});Q118=makeQuery(id+"F0.imprint","IMPRINT",FACE,{"disambiguationData":[TD([[makeQuery(id+"F0.imprint","IMPRINT",EDGE,{"disambiguationData":[TD([[subQ4,1.0]])],"derivedFrom":subQ3}),1.0]])]});}
            var Q119;
            {var subQ1=sQuery(id+"F0.wireOp",EDGE,"E9");var subQ3=sQuery(id+"F0.wireOp",EDGE,"E161");var subQ4=makeQuery(id+"F0.imprint","INTERSECT",VERTEX,{"derivedFrom":[subQ1,subQ3]});Q119=makeQuery(id+"F0.imprint","IMPRINT",FACE,{"disambiguationData":[TD([[makeQuery(id+"F0.imprint","IMPRINT",EDGE,{"disambiguationData":[TD([[subQ4,1.0]])],"derivedFrom":subQ3}),1.0]])]});}
            extrude(context, id + "F1", {"entities" : qUnion([Q0, Q1, Q2, Q3, Q4, Q5, Q6, Q7, Q8, Q9, Q10, Q11, Q12, Q13, Q14, Q15, Q16, Q17, Q18, Q19, Q20, Q21, Q22, Q23, Q24, Q25, Q26, Q27, Q28, Q29, Q30, Q31, Q32, Q33, Q34, Q35, Q36, Q37, Q38, Q39, Q40, Q41, Q42, Q43, Q44, Q45, Q46, Q47, Q48, Q49, Q50, Q51, Q52, Q53, Q54, Q55, Q56, Q57, Q58, Q59, Q60, Q61, Q62, Q63, Q64, Q65, Q66, Q67, Q68, Q69, Q70, Q71, Q72, Q73, Q74, Q75, Q76, Q77, Q78, Q79, Q80, Q81, Q82, Q83, Q84, Q85, Q86, Q87, Q88, Q89, Q90, Q91, Q92, Q93, Q94, Q95, Q96, Q97, Q98, Q99, Q100, Q101, Q102, Q103, Q104, Q105, Q106, Q107, Q108, Q109, Q110, Q111, Q112, Q113, Q114, Q115, Q116, Q117, Q118, Q119]), "depth" : 4 * mm, "offsetDistance" : 25 * mm});
        }
    });
